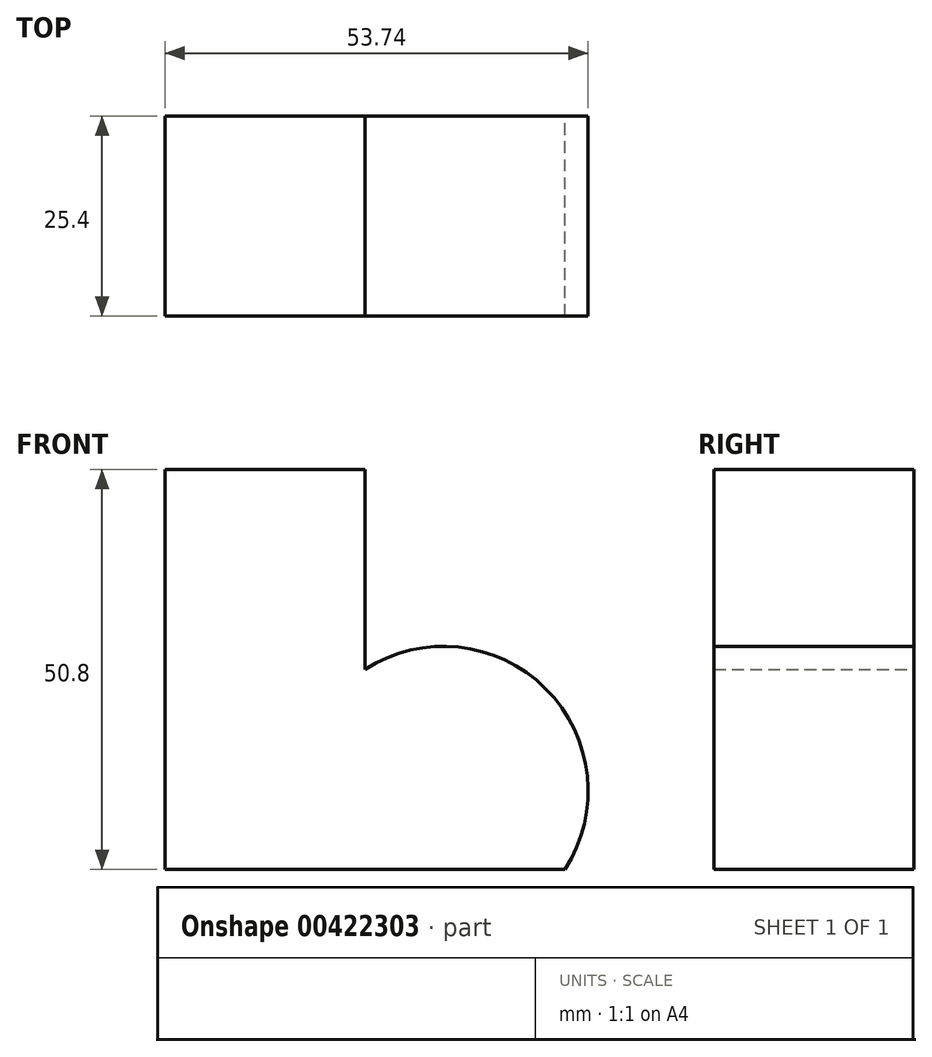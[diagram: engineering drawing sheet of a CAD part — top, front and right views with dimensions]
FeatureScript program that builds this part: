
annotation { "Feature Type Name" : "Feature", "Feature Type Description" : "" }
export const myFeature = defineFeature(function(context is Context, id is Id, definition is map)
    precondition{}
    {
        {
            var Q0;
            Q0=qCreatedBy(makeId("Front.planeOp"),FACE);
            var sketch = newSketch(context, id + "F0", { "sketchPlane" : qUnion([Q0])});
            skLineSegment(sketch, "E0", {"start": v(-64.11, -19.1) * mm, "end": v(-13.31, -19.1) * mm});
            skLineSegment(sketch, "E1", {"start": v(-64.11, -19.1) * mm, "end": v(-64.11, 31.7) * mm});
            skLineSegment(sketch, "E2", {"start": v(-64.11, 31.7) * mm, "end": v(-38.71, 31.7) * mm});
            skLineSegment(sketch, "E3", {"start": v(-38.71, 31.7) * mm, "end": v(-38.71, 6.3) * mm});
            skArc(sketch, "E4", {"start": v(-13.31, -19.1) * mm, "mid": v(-15.75, 3.85) * mm, "end": v(-38.71, 6.3) * mm});
            skSolve(sketch);
        }
        {
            var Q0;
            Q0 = qSketchRegion(id + "F0", true);
            extrude(context, id + "F1", {"entities" : qUnion([Q0]), "depth" : 25.4 * mm});
        }
    });
